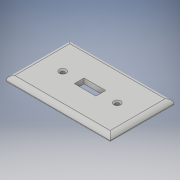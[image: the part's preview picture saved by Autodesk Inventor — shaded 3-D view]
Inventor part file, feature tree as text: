
AUTODESK INVENTOR PART (.ipt)
format: ipt  version: 2019 (Build 230136000, 136)  size: 126,464 bytes
history: native  units: mm
features: sketch x3, extrude x2, hole x1, fillet x1, projected_geometry x1
ambient origin geometry x8: Origin, YZ Plane, XZ Plane, XY Plane, X Axis, Y Axis, Z Axis, Center Point
bodies: Solid1 (feature_tree)
feature tree (8):
  extrude  "Extrusion1"  Depth=69.5mm
  extrude  "Extrusion2"  Depth=45.0mm
  hole  "Hole1"  [1 undecoded]
  fillet  "Fillet1"  Radius=18.0mm
  sketch  "Sketch1"  dims[d0=113.5mm d1=69.5mm]
  sketch  "Sketch2"  dims[d2=5.5mm d3=0.0mm d4=45.0mm]
  projected_geometry  "Projected Loop1"
  sketch  "Sketch3"  dims[d5=29.5mm d6=50.5mm d7=0.0mm d8=18.0mm d9=4.5mm d10=6.0mm d11=7.5mm d12=2.0mm d13=90.0deg d14=10.0mm d15=20.594885mm d16=4.75mm]
note: 1 required parameter value undecoded (feature->parameter linkage not recoverable at this tier; creation-order binding heuristic only, values carry confidence <= 0.55)
